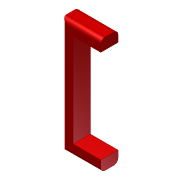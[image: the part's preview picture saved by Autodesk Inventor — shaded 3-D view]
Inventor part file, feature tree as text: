
AUTODESK INVENTOR PART (.ipt)
format: ipt  version: 2012 (Build 160160000, 160)  size: 90,112 bytes
history: native  units: in
note: dims shown in document units (in); Inventor stores cm internally (conversion verified against a paired STEP export)
features: extrude x1, fillet x1, sketch x1
ambient origin geometry x8: Origin, YZ Plane, XZ Plane, XY Plane, X Axis, Y Axis, Z Axis, Center Point
bodies: Solid1 (feature_tree)
feature tree (3):
  extrude  "Extrusion1"  Depth=3.25in
  fillet  "Fillet1"  Radius=8.0in
  sketch  "Sketch1"  dims[d0=3.25in d1=3.25in d3=8.0in d4=8.0in d5=27.0in d6=3.25in d7=5.0in d8=0.0in d9=1.25in]
